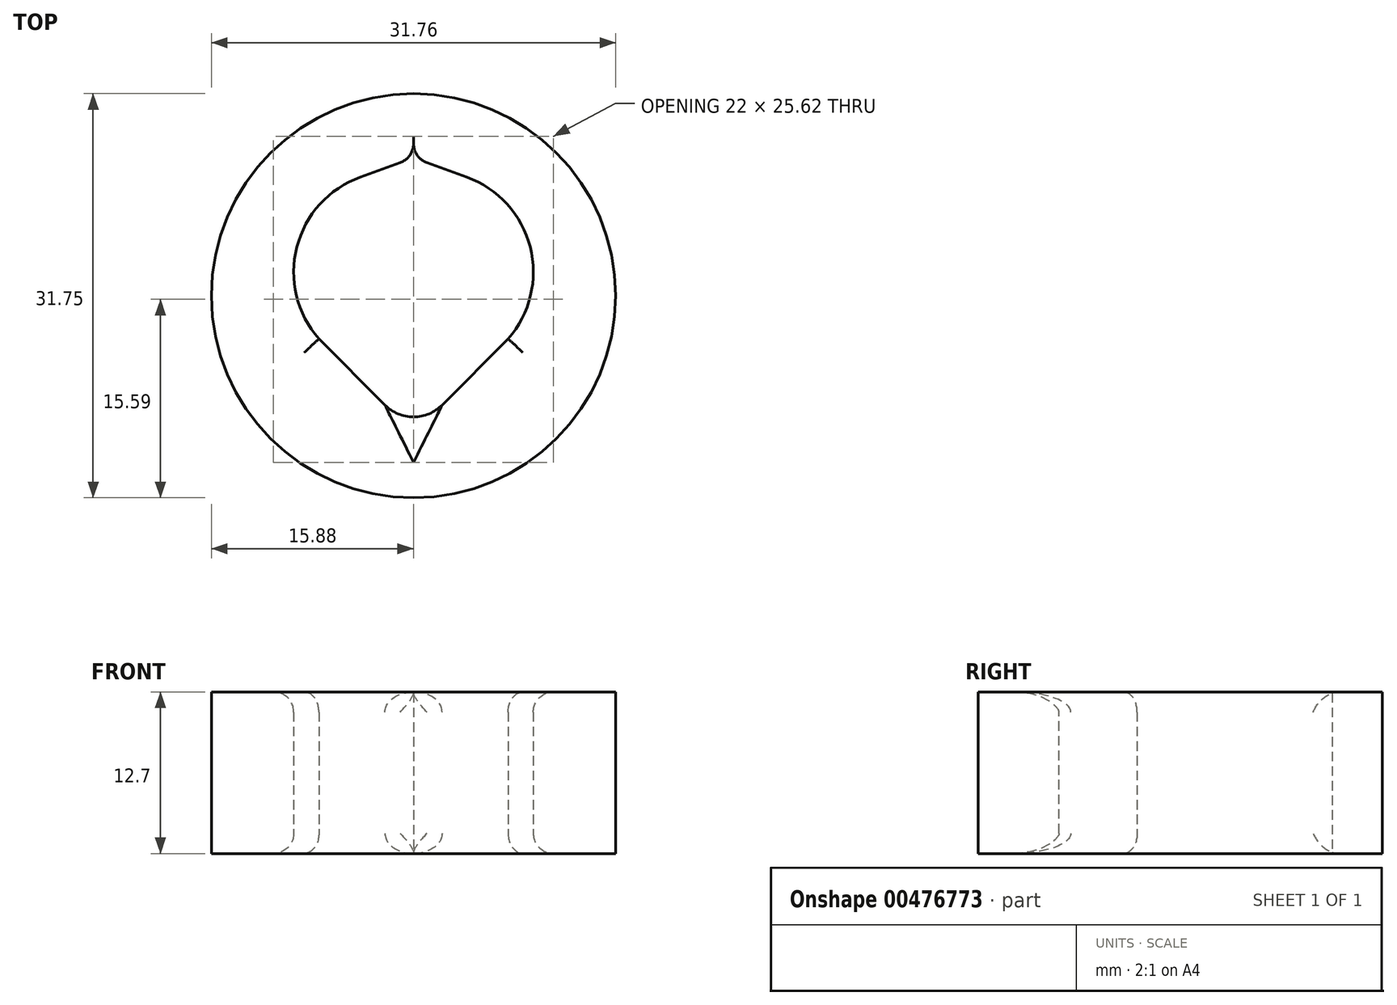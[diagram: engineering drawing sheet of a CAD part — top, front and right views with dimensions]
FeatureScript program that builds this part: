
annotation { "Feature Type Name" : "Feature", "Feature Type Description" : "" }
export const myFeature = defineFeature(function(context is Context, id is Id, definition is map)
    precondition{}
    {
        {
            var Q0;
            Q0=qCreatedBy(makeId("Top.planeOp"),FACE);
            var sketch = newSketch(context, id + "F0", { "sketchPlane" : qUnion([Q0])});
            skLineSegment(sketch, "E0.0", {"start": v(-11.68, 1.02) * mm, "end": v(0, 12.7) * mm, "construction": true});
            skPoint(sketch, "E0.0.midPoint", {"position": v(-5.84, 6.86) * mm});
            skArc(sketch, "E1", {"start": v(-4.18, 7.46) * mm, "mid": v(-9.16, 1.97) * mm, "end": v(-7.44, -5.24) * mm});
            skLineSegment(sketch, "E2", {"start": v(-5.84, 6.86) * mm, "end": v(0, 8.98) * mm});
            skLineSegment(sketch, "E3", {"start": v(0, -12.7) * mm, "end": v(-7.44, -5.24) * mm});
            skLineSegment(sketch, "E4", {"start": v(0, 14.02) * mm, "end": v(0, 8.98) * mm});
            skPoint(sketch, "E5.orphan", {"position": v(7.44, -5.24) * mm});
            skPoint(sketch, "E6.orphan", {"position": v(13.72, 0) * mm});
            skPoint(sketch, "E7.orphan", {"position": v(0, -12.7) * mm});
            skPoint(sketch, "E8.orphan", {"position": v(4.18, 7.46) * mm});
            skPoint(sketch, "E9.orphan", {"position": v(5.84, 6.86) * mm});
            skArc(sketch, "E10.trimOffspring", {"start": v(0, 8.98) * mm, "mid": v(-8.98, 0) * mm, "end": v(0, -8.98) * mm, "construction": true});
            skPoint(sketch, "E11.MirrorCS.end.orphan", {"position": v(0, 8.98) * mm});
            skLineSegment(sketch, "E12", {"start": v(0, 8.98) * mm, "end": v(0, -12.7) * mm, "construction": true});
            skArc(sketch, "E13", {"start": v(0, 14.02) * mm, "mid": v(-15.87, -1.86) * mm, "end": v(0, -17.73) * mm});
            skLineSegment(sketch, "E14", {"start": v(0, -12.7) * mm, "end": v(0, -17.73) * mm});
            skSolve(sketch);
        }
        {
            var Q0;
            {var subQ2=sQuery(id+"F0.wireOp",EDGE,"E1");Q0=makeQuery(id+"F0.imprint","IMPRINT",FACE,{"disambiguationData":[TD([[makeQuery(id+"F0.imprint","IMPRINT",EDGE,{"derivedFrom":subQ2}),-1.0]])]});}
            extrude(context, id + "F1", {"entities" : qUnion([Q0]), "endBound" : BoundingType.SYMMETRIC, "depth" : 12.7 * mm});
        }
        {
            var Q0;
            Q0=makeQuery(id+"F1.opExtrude","CAP_EDGE",EDGE,{"disambiguationData":[OSD([sQuery(id+"F0.wireOp",EDGE,"E1")])],"isStart":false});
            var Q1;
            Q1=makeQuery(id+"F1.opExtrude","CAP_EDGE",EDGE,{"disambiguationData":[OSD([sQuery(id+"F0.wireOp",EDGE,"E2")])],"isStart":false});
            var Q2;
            Q2=makeQuery(id+"F1.opExtrude","CAP_EDGE",EDGE,{"disambiguationData":[OSD([sQuery(id+"F0.wireOp",EDGE,"E3")])],"isStart":false});
            var Q3;
            Q3=makeQuery(id+"F1.opExtrude","CAP_EDGE",EDGE,{"disambiguationData":[OSD([sQuery(id+"F0.wireOp",EDGE,"21dcd32a-e958-4294-8a90-417faaac76840.MirrorCS")])],"isStart":false});
            var Q4;
            Q4=makeQuery(id+"F1.opExtrude","CAP_EDGE",EDGE,{"disambiguationData":[OSD([sQuery(id+"F0.wireOp",EDGE,"76ced346-ce6b-44ad-8c8c-2f8f2be17f2d0.MirrorCS")])],"isStart":false});
            var Q5;
            Q5=makeQuery(id+"F1.opExtrude","CAP_EDGE",EDGE,{"disambiguationData":[OSD([sQuery(id+"F0.wireOp",EDGE,"E11.MirrorCS")])],"isStart":false});
            var Q6;
            Q6=makeQuery(id+"F1.opExtrude","CAP_EDGE",EDGE,{"disambiguationData":[OSD([sQuery(id+"F0.wireOp",EDGE,"E11.MirrorCS")])],"isStart":true});
            var Q7;
            Q7=makeQuery(id+"F1.opExtrude","CAP_EDGE",EDGE,{"disambiguationData":[OSD([sQuery(id+"F0.wireOp",EDGE,"76ced346-ce6b-44ad-8c8c-2f8f2be17f2d0.MirrorCS")])],"isStart":true});
            var Q8;
            Q8=makeQuery(id+"F1.opExtrude","CAP_EDGE",EDGE,{"disambiguationData":[OSD([sQuery(id+"F0.wireOp",EDGE,"21dcd32a-e958-4294-8a90-417faaac76840.MirrorCS")])],"isStart":true});
            var Q9;
            Q9=makeQuery(id+"F1.opExtrude","CAP_EDGE",EDGE,{"disambiguationData":[OSD([sQuery(id+"F0.wireOp",EDGE,"E3")])],"isStart":true});
            var Q10;
            Q10=makeQuery(id+"F1.opExtrude","CAP_EDGE",EDGE,{"disambiguationData":[OSD([sQuery(id+"F0.wireOp",EDGE,"E1")])],"isStart":true});
            var Q11;
            Q11=makeQuery(id+"F1.opExtrude","CAP_EDGE",EDGE,{"disambiguationData":[OSD([sQuery(id+"F0.wireOp",EDGE,"E2")])],"isStart":true});
            fillet(context, id + "F2", {"entities" : qUnion([Q0, Q1, Q2, Q3, Q4, Q5, Q6, Q7, Q8, Q9, Q10, Q11]), "radius" : 1.59 * mm, "allowEdgeOverflow" : false});
        }
        {
            var Q0;
            Q0=makeQuery(id+"F1.opExtrude","SWEPT_EDGE",EDGE,{"disambiguationData":[OSD([sQuery(id+"F0.wireOp",EDGE,"E2"),sQuery(id+"F0.wireOp",EDGE,"E4")])]});
            fillet(context, id + "F3", {"entities" : qUnion([Q0]), "radius" : 1.59 * mm, "allowEdgeOverflow" : false});
        }
        {
            var Q0;
            Q0=makeQuery(id+"F1.opExtrude","SWEPT_BODY",BODY,{"disambiguationData":[OSD([sQuery(id+"F0.wireOp",EDGE,"E1"),sQuery(id+"F0.wireOp",EDGE,"E2"),sQuery(id+"F0.wireOp",EDGE,"Ckv9YzEm-5UcW-s07E-b819-D4WlfnAO0HpF"),sQuery(id+"F0.wireOp",EDGE,"E3"),sQuery(id+"F0.wireOp",EDGE,"E4"),sQuery(id+"F0.wireOp",EDGE,"bacf0e5b-cdae-4414-b894-c89993d3772e.trimOffspring")])]});
            var Q1;
            Q1=qCreatedBy(makeId("Right.planeOp"),FACE);
            mirror(context, id + "F4", {"operationType" : NewBodyOperationType.ADD, "entities" : qUnion([Q0]), "mirrorPlane" : qUnion([Q1])});
        }
        {
            var Q0;
            {var subQ0=makeQuery(id+"F1.opExtrude","SWEPT_EDGE",EDGE,{"disambiguationData":[OSD([sQuery(id+"F0.wireOp",EDGE,"E3"),sQuery(id+"F0.wireOp",EDGE,"bacf0e5b-cdae-4414-b894-c89993d3772e.trimOffspring")])]});Q0=makeQuery(id+"F4.boolean.opBoolean","MERGE",EDGE,{"derivedFrom":[subQ0,makeQuery(id+"F4.opPattern","COPY",EDGE,{"derivedFrom":subQ0,"instanceName":"1"})]});}
            fillet(context, id + "F5", {"entities" : qUnion([Q0]), "radius" : 3.17 * mm, "tangentPropagation" : true, "allowEdgeOverflow" : false});
        }
    });
